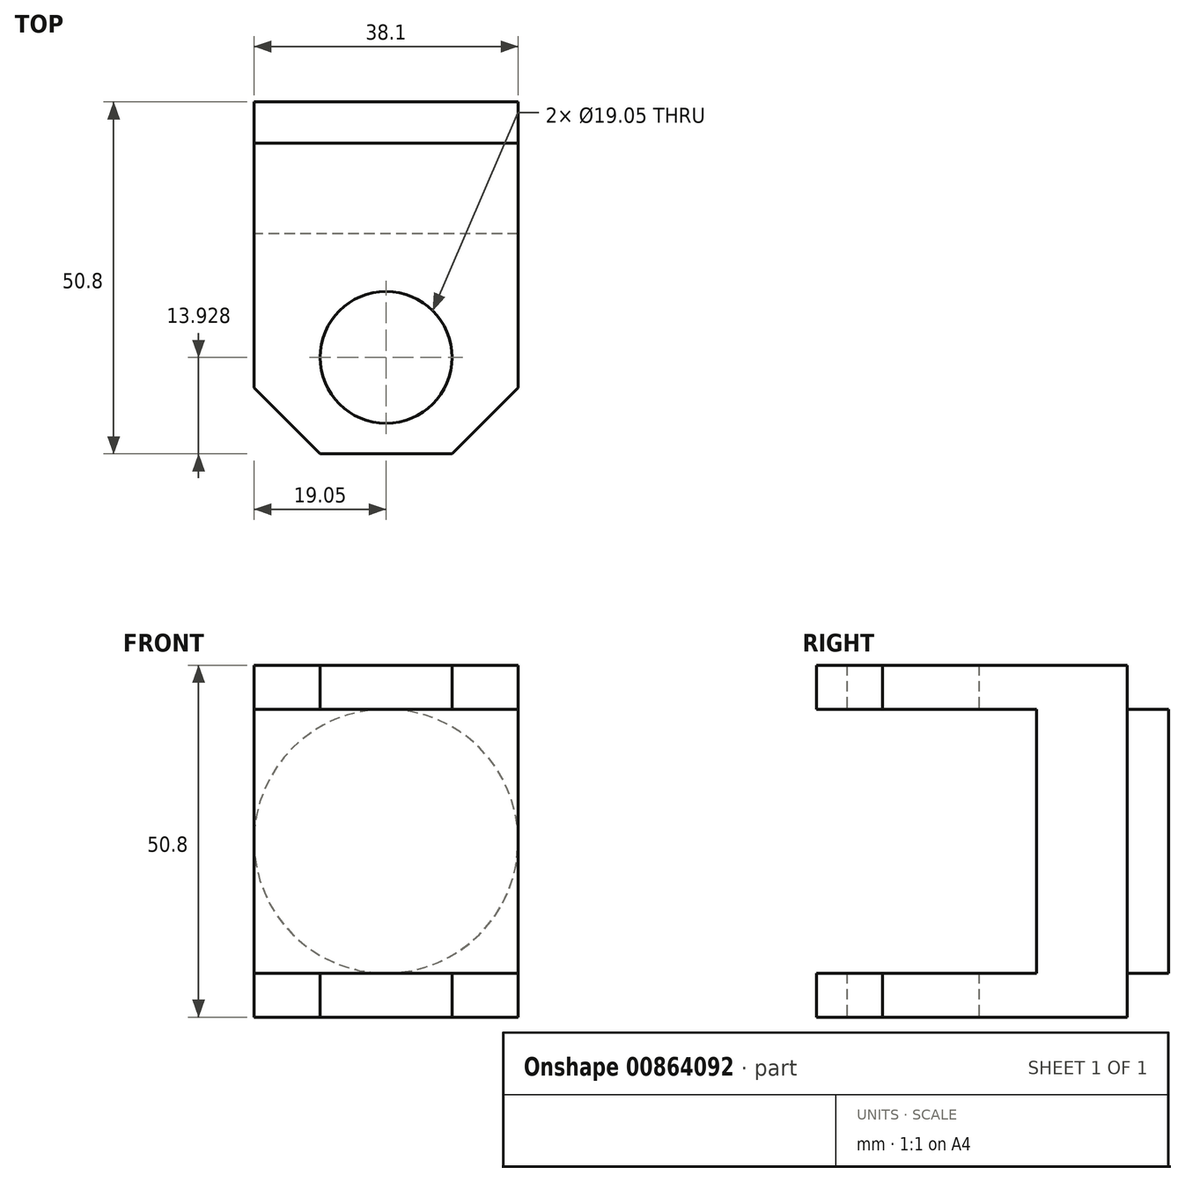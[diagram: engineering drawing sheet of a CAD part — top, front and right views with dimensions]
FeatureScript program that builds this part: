
annotation { "Feature Type Name" : "Feature", "Feature Type Description" : "" }
export const myFeature = defineFeature(function(context is Context, id is Id, definition is map)
    precondition{}
    {
        {
            var Q0;
            Q0=qCreatedBy(makeId("Front.planeOp"),FACE);
            var sketch = newSketch(context, id + "F0", { "sketchPlane" : qUnion([Q0])});
            skCircle(sketch, "E0", {"center": v(0, 0) * mm, "radius": 19.05 * mm});
            skSolve(sketch);
        }
        {
            var Q0;
            Q0=qCreatedBy(makeId("Right.planeOp"),FACE);
            var sketch = newSketch(context, id + "F1", { "sketchPlane" : qUnion([Q0])});
            skLineSegment(sketch, "E1.bottom", {"start": v(-38.1, -25.4) * mm, "end": v(6.73, -25.4) * mm});
            skLineSegment(sketch, "E1.top", {"start": v(-38.1, 25.4) * mm, "end": v(6.73, 25.4) * mm});
            skLineSegment(sketch, "E1.left", {"start": v(-38.1, -25.4) * mm, "end": v(-38.1, -19.05) * mm});
            skPoint(sketch, "E1.middle", {"position": v(0, 0) * mm});
            skLineSegment(sketch, "E2.bottom", {"start": v(-6.35, -19.05) * mm, "end": v(-38.1, -19.05) * mm});
            skLineSegment(sketch, "E2.top", {"start": v(-6.35, 19.05) * mm, "end": v(-38.1, 19.05) * mm});
            skLineSegment(sketch, "E2.left", {"start": v(-6.35, -19.05) * mm, "end": v(-6.35, 19.05) * mm});
            skPoint(sketch, "E2.middle", {"position": v(-38.1, 0) * mm});
            skLineSegment(sketch, "E3", {"start": v(6.73, 25.4) * mm, "end": v(6.73, -25.4) * mm});
            skPoint(sketch, "E1.right.end.orphan", {"position": v(38.1, 25.4) * mm});
            skPoint(sketch, "E1.right.start.orphan", {"position": v(38.1, -25.4) * mm});
            skLineSegment(sketch, "E4.trimOffspring", {"start": v(-38.1, 19.05) * mm, "end": v(-38.1, 25.4) * mm});
            skPoint(sketch, "E5.orphan", {"position": v(-69.85, -19.05) * mm});
            skPoint(sketch, "E6.orphan", {"position": v(-69.85, 19.05) * mm});
            skSolve(sketch);
        }
        {
            var Q0;
            Q0=makeQuery(id+"F1.imprint","IMPRINT",FACE,{"disambiguationData":[TD([[makeQuery(id+"F1.imprint","IMPRINT",EDGE,{"derivedFrom":sQuery(id+"F1.wireOp",EDGE,"E1.bottom")}),1.0]])]});
            extrude(context, id + "F2", {"entities" : qUnion([Q0]), "depth" : 38.1 * mm, "offsetDistance" : 25.4 * mm, "symmetric" : true});
        }
        {
            var Q0;
            Q0=makeQuery(id+"F2.opExtrude","SWEPT_FACE",FACE,{"disambiguationData":[OSD([sQuery(id+"F1.wireOp",EDGE,"E1.bottom")])]});
            var sketch = newSketch(context, id + "F3", { "sketchPlane" : qUnion([Q0])});
            skCircle(sketch, "E7", {"center": v(0, 24.17) * mm, "radius": 9.53 * mm});
            skSolve(sketch);
        }
        {
            var Q0;
            Q0=makeQuery(id+"F3.imprint","IMPRINT",FACE,{"disambiguationData":[TD([[makeQuery(id+"F3.imprint","IMPRINT",EDGE,{"derivedFrom":sQuery(id+"F3.wireOp",EDGE,"E7")}),1.0]])]});
            extrude(context, id + "F4", {"entities" : qUnion([Q0]), "operationType" : NewBodyOperationType.REMOVE, "endBound" : BoundingType.THROUGH_ALL, "oppositeDirection" : true, "depth" : 25.4 * mm, "offsetDistance" : 25.4 * mm});
        }
        {
            var Q0;
            Q0=makeQuery(id+"F2.opExtrude","CAP_EDGE",EDGE,{"disambiguationData":[OSD([sQuery(id+"F1.wireOp",EDGE,"E4.trimOffspring")])],"isStart":true});
            var Q1;
            Q1=makeQuery(id+"F2.opExtrude","CAP_EDGE",EDGE,{"disambiguationData":[OSD([sQuery(id+"F1.wireOp",EDGE,"E4.trimOffspring")])],"isStart":false});
            var Q2;
            Q2=makeQuery(id+"F2.opExtrude","CAP_EDGE",EDGE,{"disambiguationData":[OSD([sQuery(id+"F1.wireOp",EDGE,"E1.left")])],"isStart":true});
            var Q3;
            Q3=makeQuery(id+"F2.opExtrude","CAP_EDGE",EDGE,{"disambiguationData":[OSD([sQuery(id+"F1.wireOp",EDGE,"E1.left")])],"isStart":false});
            chamfer(context, id + "F5", {"entities" : qUnion([Q0, Q1, Q2, Q3]), "width" : 9.52 * mm, "tangentPropagation" : true});
        }
        {
            var Q0;
            Q0 = qSketchRegion(id + "F0", true);
            extrude(context, id + "F6", {"entities" : qUnion([Q0]), "operationType" : NewBodyOperationType.ADD, "oppositeDirection" : true, "depth" : 12.7 * mm, "offsetDistance" : 25.4 * mm});
        }
    });
